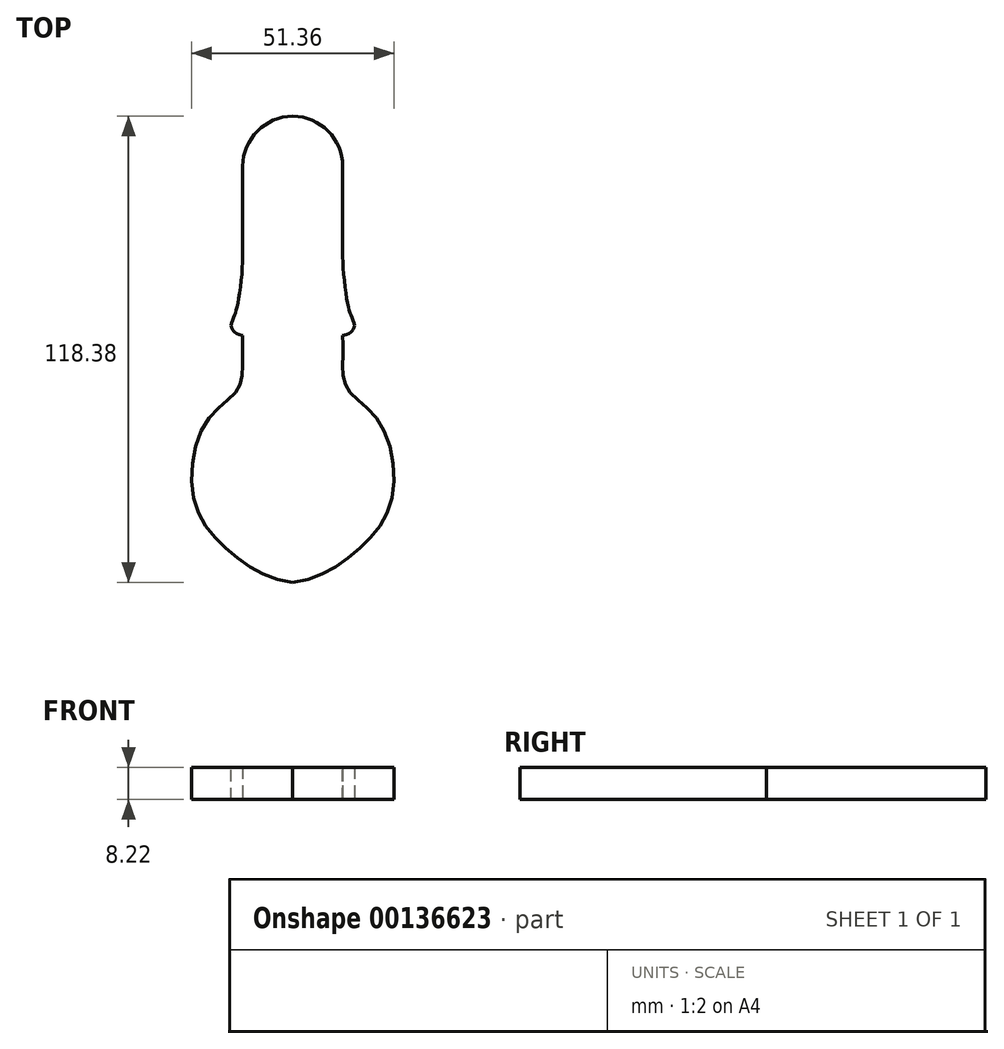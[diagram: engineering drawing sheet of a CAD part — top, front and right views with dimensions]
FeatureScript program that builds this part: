
annotation { "Feature Type Name" : "Feature", "Feature Type Description" : "" }
export const myFeature = defineFeature(function(context is Context, id is Id, definition is map)
    precondition{}
    {
        {
            var Q0;
            Q0=qCreatedBy(makeId("Top.planeOp"),FACE);
            var sketch = newSketch(context, id + "F0", { "sketchPlane" : qUnion([Q0])});
            skLineSegment(sketch, "E0.bottom", {"start": v(-4.05, 6.46) * mm, "end": v(8.65, 6.46) * mm});
            skLineSegment(sketch, "E0.top", {"start": v(-4.05, -34.18) * mm, "end": v(-3.3, -34.18) * mm});
            skLineSegment(sketch, "E0.left", {"start": v(-4.05, 6.46) * mm, "end": v(-4.05, -34.18) * mm});
            skLineSegment(sketch, "E0.right", {"start": v(21.35, 6.46) * mm, "end": v(21.35, -34.18) * mm});
            skLineSegment(sketch, "E1", {"start": v(8.65, 6.46) * mm, "end": v(8.65, -73.4) * mm, "construction": true});
            skFitSpline(sketch, "E2", {"points": [v(-3.3, -34.18) * mm, v(-4.05, -36.5) * mm, v(-4.05, -44.15) * mm, v(-5.5, -50.43) * mm, v(-13.28, -58.4) * mm, v(-16.37, -78.41) * mm, v(-6.77, -91.94) * mm, v(8.65, -99.22) * mm], "startDerivative": vector(-18.48, -24.4) * mm, "endDerivative": vector(99, -7.24) * mm});
            skFitSpline(sketch, "E3.MirrorCS", {"points": [v(20.6, -34.18) * mm, v(21.35, -36.5) * mm, v(21.35, -44.15) * mm, v(22.81, -50.43) * mm, v(30.58, -58.4) * mm, v(33.67, -78.41) * mm, v(24.07, -91.94) * mm, v(8.65, -99.22) * mm], "startDerivative": vector(18.48, -24.4) * mm, "endDerivative": vector(-99, -7.24) * mm});
            skArc(sketch, "E4", {"start": v(21.35, 6.46) * mm, "mid": v(8.65, 19.16) * mm, "end": v(-4.05, 6.46) * mm});
            skLineSegment(sketch, "E5.trimOffspring", {"start": v(8.65, -34.18) * mm, "end": v(21.35, -34.18) * mm});
            skFitSpline(sketch, "E6", {"points": [v(-4.05, -36.5) * mm, v(-6.28, -35.55) * mm, v(-6.98, -34.18) * mm, v(-6.28, -31.7) * mm, v(-5.35, -28.64) * mm, v(-4.05, -16.55) * mm], "startDerivative": vector(-28.14, 5.5) * mm, "endDerivative": vector(0, 28.69) * mm});
            skFitSpline(sketch, "E7.MirrorCS", {"points": [v(21.35, -36.5) * mm, v(23.59, -35.55) * mm, v(24.28, -34.18) * mm, v(23.59, -31.7) * mm, v(22.66, -28.64) * mm, v(21.35, -16.55) * mm], "startDerivative": vector(28.14, 5.5) * mm, "endDerivative": vector(0, 28.69) * mm});
            skSolve(sketch);
        }
        {
            var Q0;
            {var subQ0=sQuery(id+"F0.wireOp",EDGE,"E0.top");Q0=makeQuery(id+"F0.imprint","IMPRINT",FACE,{"disambiguationData":[TD([[makeQuery(id+"F0.imprint","IMPRINT",EDGE,{"derivedFrom":subQ0}),-1.0]])]});}
            var Q1;
            {var subQ5=sQuery(id+"F0.wireOp",EDGE,"E0.top");Q1=makeQuery(id+"F0.imprint","IMPRINT",FACE,{"disambiguationData":[TD([[makeQuery(id+"F0.imprint","IMPRINT",EDGE,{"derivedFrom":subQ5}),1.0]])]});}
            var Q2;
            {var subQ3=sQuery(id+"F0.wireOp",EDGE,"E7.MirrorCS");Q2=makeQuery(id+"F0.imprint","IMPRINT",FACE,{"disambiguationData":[TD([[makeQuery(id+"F0.imprint","IMPRINT",EDGE,{"derivedFrom":subQ3}),1.0]])]});}
            extrude(context, id + "F1", {"entities" : qUnion([Q0, Q1, Q2]), "depth" : 8.22 * mm});
        }
    });
